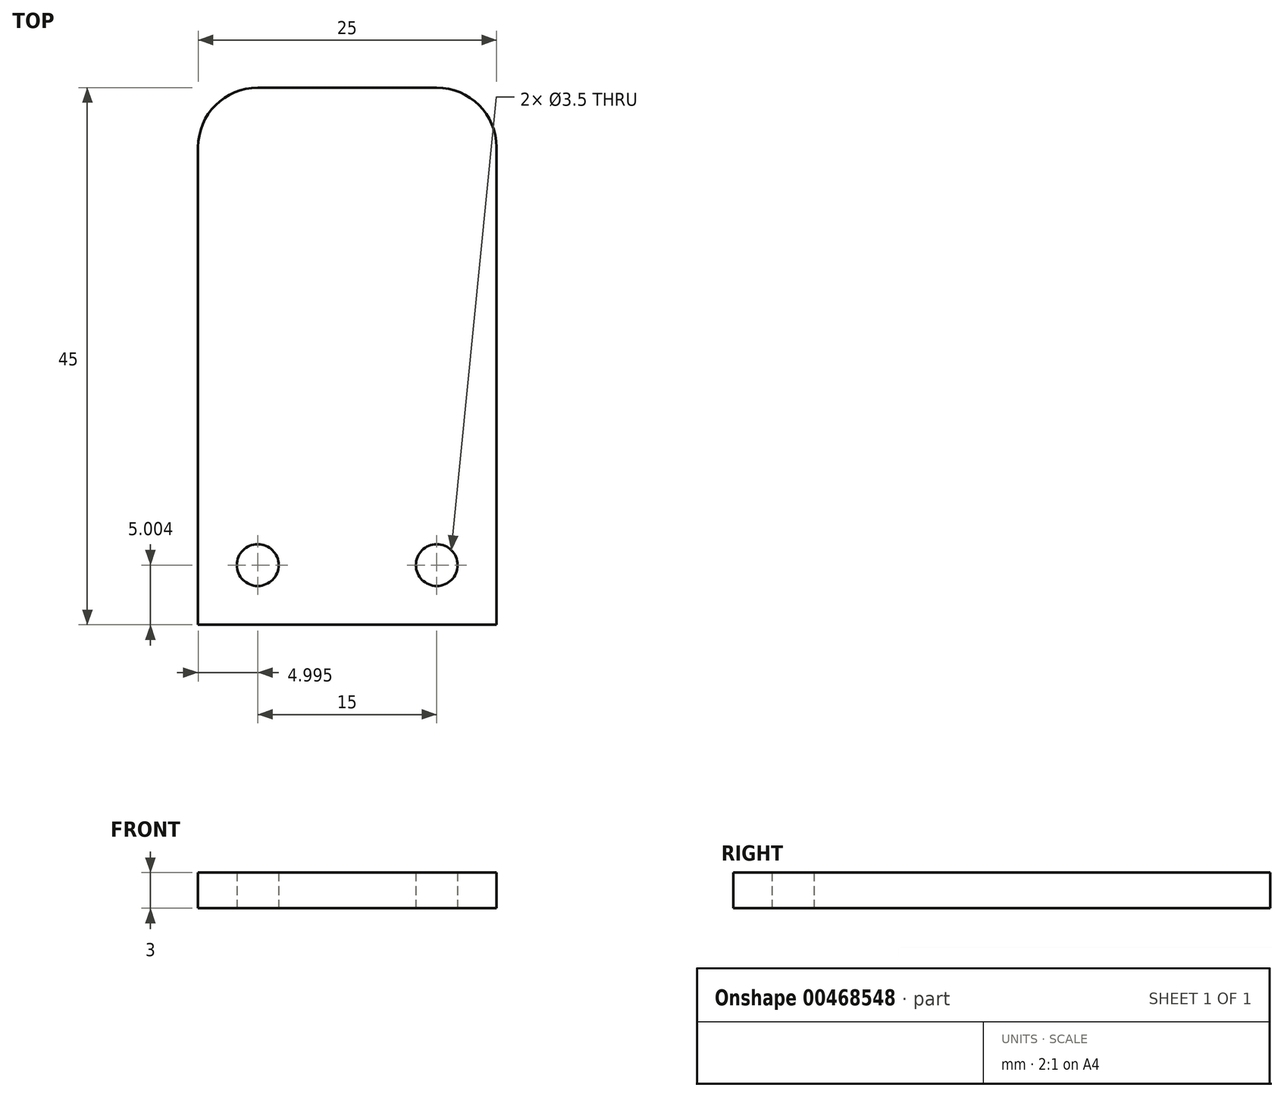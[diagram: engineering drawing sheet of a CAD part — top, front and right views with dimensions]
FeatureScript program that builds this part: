
annotation { "Feature Type Name" : "Feature", "Feature Type Description" : "" }
export const myFeature = defineFeature(function(context is Context, id is Id, definition is map)
    precondition{}
    {
        {
            var Q0;
            Q0=qCreatedBy(makeId("Top.planeOp"),FACE);
            var sketch = newSketch(context, id + "F0", { "sketchPlane" : qUnion([Q0])});
            skLineSegment(sketch, "E0.bottom", {"start": v(-15.33, 38.35) * mm, "end": v(9.67, 38.35) * mm});
            skLineSegment(sketch, "E0.top", {"start": v(-15.33, -6.65) * mm, "end": v(9.67, -6.65) * mm});
            skLineSegment(sketch, "E0.left", {"start": v(-15.33, 38.35) * mm, "end": v(-15.33, -6.65) * mm});
            skLineSegment(sketch, "E0.right", {"start": v(9.67, 38.35) * mm, "end": v(9.67, -6.65) * mm});
            skLineSegment(sketch, "E1", {"start": v(-15.33, -1.65) * mm, "end": v(9.67, -1.65) * mm, "construction": true});
            skCircle(sketch, "E2", {"center": v(-10.33, -1.65) * mm, "radius": 1.75 * mm});
            skCircle(sketch, "E3", {"center": v(4.67, -1.65) * mm, "radius": 1.75 * mm});
            skSolve(sketch);
        }
        {
            var Q0;
            Q0=makeQuery(id+"F0.imprint","IMPRINT",FACE,{"disambiguationData":[TD([[makeQuery(id+"F0.imprint","IMPRINT",EDGE,{"derivedFrom":sQuery(id+"F0.wireOp",EDGE,"E0.bottom")}),-1.0]])]});
            extrude(context, id + "F1", {"entities" : qUnion([Q0]), "depth" : 3 * mm, "offsetDistance" : 25 * mm});
        }
        {
            var Q0;
            Q0=makeQuery(id+"F1.opExtrude","SWEPT_EDGE",EDGE,{"disambiguationData":[OSD([sQuery(id+"F0.wireOp",EDGE,"E0.bottom"),sQuery(id+"F0.wireOp",EDGE,"E0.right")])]});
            var Q1;
            Q1=makeQuery(id+"F1.opExtrude","SWEPT_EDGE",EDGE,{"disambiguationData":[OSD([sQuery(id+"F0.wireOp",EDGE,"E0.bottom"),sQuery(id+"F0.wireOp",EDGE,"E0.left")])]});
            fillet(context, id + "F2", {"entities" : qUnion([Q0, Q1]), "radius" : 5 * mm, "tangentPropagation" : true, "allowEdgeOverflow" : false});
        }
    });
